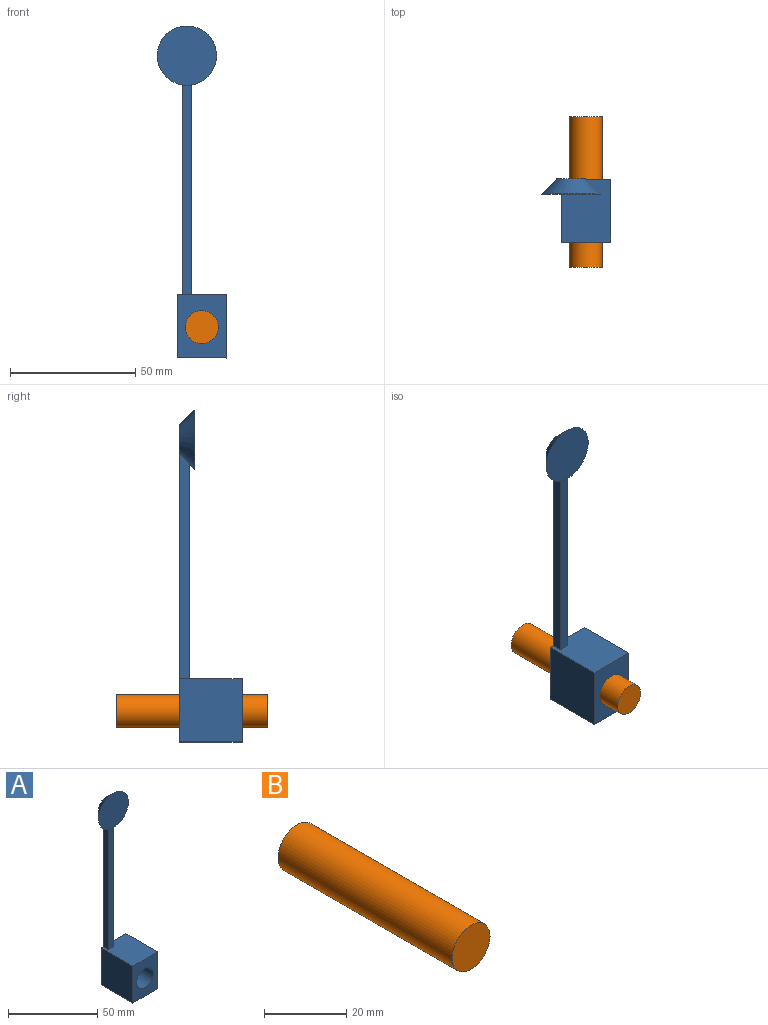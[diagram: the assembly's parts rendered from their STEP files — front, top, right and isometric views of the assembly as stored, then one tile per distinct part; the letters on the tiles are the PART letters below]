
ASSEMBLY  parts=2 mates=1
PART A: 12 faces, bbox 27.7x25x132.6 mm
  f0: plane 90.02x4mm, normal (1,0,0), area 351.7mm2, adj f2,f8,f9,f10
  f1: plane 90.02x4mm, normal (-1,0,0), area 351.7mm2, adj f2,f8,f9,f10
  f2: plane 25x19.6mm, normal (0,0,1), area 474.3mm2, adj f0,f1,f3,f6,f7,f8,f9
  f3: plane 25.21x25mm, normal (-1,0,0), area 630.2mm2, adj f2,f4,f7,f8
  f4: plane 25x19.6mm, normal (0,0,-1), area 489.9mm2, adj f3,f6,f7,f8
  f5: cylinder r=6.55mm len=25mm, axis (0,1,0), area 1029.6mm2, adj f7,f8
  f6: plane 25.21x25mm, normal (1,0,0), area 630.2mm2, adj f2,f4,f7,f8
  f7: plane 25.21x19.6mm, normal (0,-1,0), area 359mm2, adj f2,f3,f4,f5,f6
  f8: plane 126.58x21.75mm, normal (0,1,0), area 816.5mm2, adj f0,f1,f2,f3,f4,f5,f6,f10
  f9: plane 85.88x3.9mm, normal (0,-1,0), area 334.3mm2, adj f0,f1,f2,f10
  f10: cone r=5.85mm half-angle=45deg, axis (0,-1,0), area 449.4mm2, adj f0,f1,f8,f9,f11
  f11: plane 23.69x23.69mm, normal (0,-1,0), area 440.9mm2, adj f10
PART B: 3 faces, bbox 13.1x60x13.1 mm
  f0: cylinder r=6.55mm len=60mm, axis (0,1,0), area 2471.1mm2, adj f1,f2
  f1: plane 13.11x13.11mm, normal (0,-1,0), area 135mm2, adj f0
  f2: plane 13.11x13.11mm, normal (0,1,0), area 135mm2, adj f0
PLACE A rot(axis=(0,1,0),0deg) t=(8.74,10.41,-43.7)mm
PLACE B rot(axis=(0,1,0),0deg) t=(8.74,35.41,-43.7)mm
MATE slider A.f5 <-> B.f0  axis (0,1,0) through (-28.16,-14.59,-31.36)mm
